# Revit family: Hager-Vector-IP65-syst-PL-en
name_source: partatom
category: Electrical Equipment
units: mm (PartAtom-declared; Revit-internal decimal feet)

## family parameters
Cut with Voids When Loaded = No
Host = Face
Panel Configuration = Two Columns, Circuits Across
Part Type = Panelboard
Room Calculation Point = No
Round Connector Dimension = Use Diameter
Shared = No

## types (8) — shared parameters
EF000003 - Mounting method = EV000384 - Surface mounted (plaster)
EF000007 - Colour = EV000270 - Grey
EF000116 - RAL-number = 7035
EF000339 - Type of cover = EV004216 - Door
EF001596 - Material housing = EV000139 - Plastic
EF004462 - Type of closure = EV000154 - Other
EF005474 - Degree of protection (IP) = EV006421 - IP65
EF006244 - Transparent cover/door = Yes
EF006306 - With lock = Yes
EF015776 - Earthing terminal block = No
EF015777 - Neutral terminal block = No
HG000001 - Number of columns = 1
HG000002 - With door or cover = Yes
HG000003 - Range = Vector
HG000005 - Thickness = 3 mm  [stored 0.00984252 ft]
HG000006 - Flush mounted = No
HG000009 - Double swing door = No
HG000010 - Asymmetric doors = No
HG000011 - Empty rows from bottom = No
HG000017 - Distance between poles = 18 mm  [stored 0.0590551 ft]
Manufacturer = Hager
Type Comments = Vector
zero-valued in all types: Default Elevation, EF000332 - Built-in height, EF000846 - Built-in width, HG000007 - Number of empty columns, HG000008 - Number of empty rows

## per-type parameters (varying)
| type | EF000008 - Width | EF000040 - Height | EF000049 - Depth | EF000118 - With mounting plate | EF000218 - Built-in depth | EF000266 - Number of rows | EF001062 - EMC-version | EF001088 - Extension possible | EF001131 - Internal depth | EF001134 - DIN-rail | EF002950 - Width in number of modular spacings | EF009212 - Cover model | EF015941 - Signal passing door | HG000004 - Manufacturer reference | Model |
| Surface mounted IP65 W250 H350 D160 10 Modular spacings - VP20M | 250 mm  [stored 0.82021 ft] | 350 mm | 160 mm | No | 160 mm | 2 | Yes | Yes | 160 mm | Yes | 10 | EV000116 - Closed | No | VP20M | VP20M |
| Surface mounted IP65 W300 H300 D160 12 Modular spacings - VP36D | 300 mm | 300 mm | 160 mm | Yes | 160 mm | 1 | No | No | 160 mm | Yes | 12 | EV009916 - With notch | Yes | VP36D | VP36D |
| Surface mounted IP65 W300 H500 D160 12 Modular spacings - VP36AE | 300 mm | 500 mm  [stored 1.64042 ft] | 160 mm | No | 0 mm  [stored 0 ft] | 3 | Yes | Yes | 0 mm  [stored 0 ft] | No | 12 |  | No | VP36AE | VP36AE |
| Surface mounted IP65 W300 H500 D160 12 Modular spacings - VP36M | 300 mm | 500 mm  [stored 1.64042 ft] | 160 mm | No | 160 mm | 3 | Yes | Yes | 160 mm | Yes | 12 | EV000116 - Closed | No | VP36M | VP36M |
| Surface mounted IP65 W400 H400 D210 18 Modular spacings - VP54D | 400 mm  [stored 1.31234 ft] | 400 mm  [stored 1.31234 ft] | 210 mm  [stored 0.688976 ft] | Yes | 210 mm  [stored 0.688976 ft] | 1 | No | No | 210 mm  [stored 0.688976 ft] | Yes | 18 | EV009916 - With notch | Yes | VP54D | VP54D |
| Surface mounted IP65 W400 H400 D210 18 Modular spacings - VP72D | 400 mm  [stored 1.31234 ft] | 400 mm  [stored 1.31234 ft] | 210 mm  [stored 0.688976 ft] | Yes | 210 mm  [stored 0.688976 ft] | 1 | No | No | 210 mm  [stored 0.688976 ft] | Yes | 18 | EV009916 - With notch | Yes | VP72D | VP72D |
| Surface mounted IP65 W400 H500 D210 18 Modular spacings - VP54M | 400 mm  [stored 1.31234 ft] | 500 mm  [stored 1.64042 ft] | 210 mm  [stored 0.688976 ft] | No | 210 mm  [stored 0.688976 ft] | 3 | Yes | Yes | 210 mm  [stored 0.688976 ft] | Yes | 18 | EV000116 - Closed | No | VP54M | VP54M |
| Surface mounted IP65 W400 H650 D210 18 Modular spacings - VP72M | 400 mm  [stored 1.31234 ft] | 650 mm  [stored 2.13255 ft] | 210 mm  [stored 0.688976 ft] | No | 210 mm  [stored 0.688976 ft] | 4 | Yes | Yes | 210 mm  [stored 0.688976 ft] | Yes | 18 | EV000116 - Closed | No | VP72M | VP72M |

note: [stored X ft] marks values corroborated as IEEE doubles in the binary element streams (Revit-internal decimal feet)

## geometry (parser evidence)
native form markers: Sweep x17
no freeform markers — native parametric forms only
